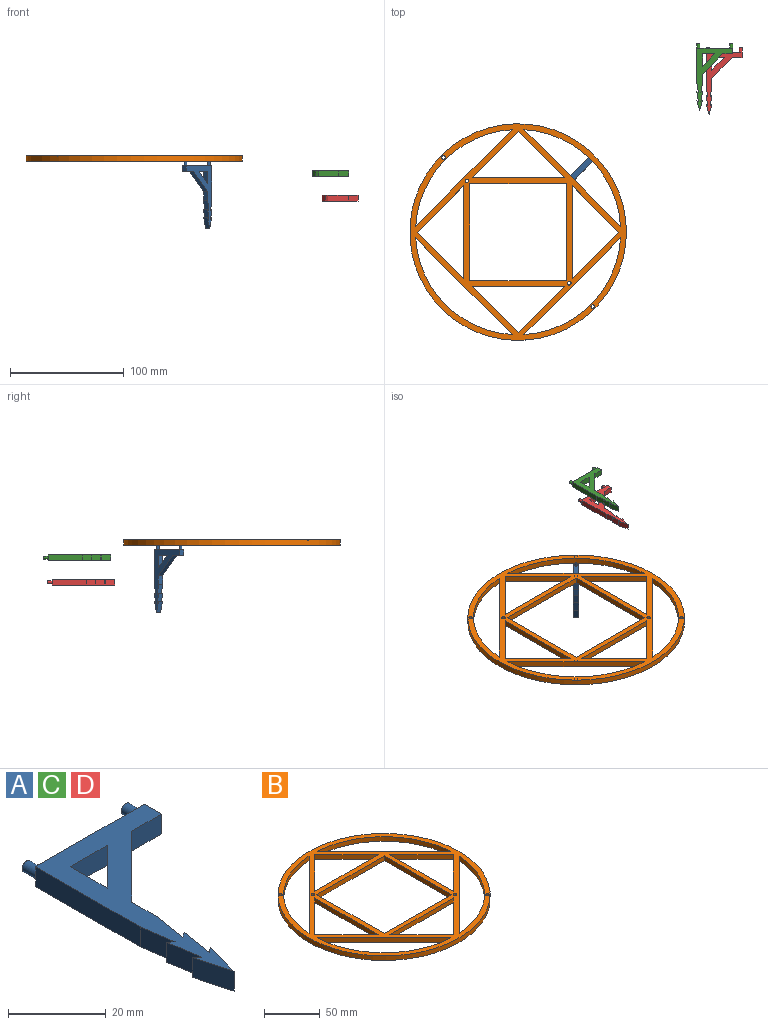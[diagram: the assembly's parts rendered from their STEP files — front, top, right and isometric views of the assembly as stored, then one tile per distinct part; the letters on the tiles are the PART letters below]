
ASSEMBLY  parts=4 mates=1
PART A: 25 faces, bbox 31.4x59x5 mm
  f0: plane 55x31.43mm, normal (0,0,1), area 463.5mm2, adj f2,f3,f4,f5,f6,f7,f8,f9
  f1: plane 55x31.43mm, normal (0,0,-1), area 463.5mm2, adj f2,f3,f4,f5,f6,f7,f8,f9
  f2: plane 7.47x5mm, normal (1,0,0), area 37.3mm2, adj f0,f1,f4,f21
  f3: plane 30.25x5mm, normal (-1,0,0), area 151.2mm2, adj f0,f1,f10,f22
  f4: plane 17.78x17.78mm, normal (0.71,-0.71,0), area 125.7mm2, adj f0,f1,f2,f5
  f5: plane 8.64x5mm, normal (0,-1,0), area 43.2mm2, adj f0,f1,f4,f6
  f6: plane 5x5mm, normal (1,0,0), area 25mm2, adj f0,f1,f5,f10
  f7: plane 10.71x5mm, normal (1,0,0), area 53.6mm2, adj f0,f1,f8,f9
  f8: plane 10.71x5mm, normal (0,-1,0), area 53.6mm2, adj f0,f1,f7,f9
  f9: plane 10.71x10.71mm, normal (-0.71,0.71,0), area 75.7mm2, adj f0,f1,f7,f8
  f10: plane 31.43x5mm, normal (0,1,0), area 146.5mm2, adj f0,f1,f3,f6,f11,f13
  f11: cylinder r=1.3mm len=4mm, axis (0,-1,0), area 32.7mm2, adj f10,f12
  f12: plane 2.6x2.6mm, normal (0,1,0), area 5.3mm2, adj f11
  f13: cylinder r=1.3mm len=4mm, axis (0,-1,0), area 32.7mm2, adj f10,f14
  f14: plane 2.6x2.6mm, normal (0,1,0), area 5.3mm2, adj f13
  f15: plane 8.81x5mm, normal (-0.99,-0.15,0), area 44.6mm2, adj f0,f1,f16,f23
  f16: plane 5x1.34mm, normal (0.67,0.74,0), area 9mm2, adj f0,f1,f15,f19
  f17: plane 5x1.38mm, normal (-0.66,0.75,0), area 9.2mm2, adj f0,f1,f18,f24
  f18: plane 8.81x5mm, normal (0.99,-0.16,0), area 44.6mm2, adj f0,f1,f17,f20
  f19: plane 9.41x5mm, normal (-0.97,-0.26,0), area 48.7mm2, adj f0,f1,f16,f24
  f20: plane 5x1.38mm, normal (-0.61,0.79,0), area 8.7mm2, adj f0,f1,f18,f21
  f21: plane 8.81x5mm, normal (0.99,-0.16,0), area 44.6mm2, adj f0,f1,f2,f20
  f22: plane 8.81x5mm, normal (-0.99,-0.15,0), area 44.6mm2, adj f0,f1,f3,f23
  f23: plane 5x1.34mm, normal (0.62,0.78,0), area 8.5mm2, adj f0,f1,f15,f22
  f24: plane 9.41x5mm, normal (0.97,-0.26,0), area 48.7mm2, adj f0,f1,f17,f19
PART B: 43 faces, bbox 190x190x5 mm
  f0: plane 190x190mm, normal (0,0,-1), area 7034.6mm2, adj f1,f2,f3,f4,f5,f6,f7,f8
  f1: plane 85x5mm, normal (0,1,0), area 425mm2, adj f0,f2,f25,f26
  f2: plane 85x5mm, normal (1,0,0), area 425mm2, adj f0,f1,f3,f26
  f3: plane 85x5mm, normal (0,-1,0), area 425mm2, adj f0,f2,f25,f26
  f4: plane 80.86x5mm, normal (-1,0,0), area 404.3mm2, adj f0,f5,f16,f26
  f5: plane 40.43x40.43mm, normal (0.71,0.71,0), area 285.9mm2, adj f0,f4,f16,f26
  f6: plane 40.43x40.43mm, normal (0.71,-0.71,0), area 285.9mm2, adj f0,f7,f17,f26
  f7: plane 40.43x40.43mm, normal (-0.71,-0.71,0), area 285.9mm2, adj f0,f6,f17,f26
  f8: cylinder r=90mm len=84.71mm, axis (0,0,-1), area 655.4mm2, adj f0,f18,f26
  f9: plane 40.43x40.43mm, normal (0.71,0.71,0), area 285.9mm2, adj f0,f10,f20,f26
  f10: plane 80.86x5mm, normal (0,-1,0), area 404.3mm2, adj f0,f9,f20,f26
  f11: cylinder r=90mm len=84.71mm, axis (0,0,-1), area 655.4mm2, adj f0,f21,f26
  f12: plane 40.43x40.43mm, normal (-0.71,-0.71,0), area 285.9mm2, adj f0,f13,f22,f26
  f13: plane 40.43x40.43mm, normal (-0.71,0.71,0), area 285.9mm2, adj f0,f12,f22,f26
  f14: cylinder r=90mm len=84.71mm, axis (0,0,-1), area 655.4mm2, adj f0,f23,f26
  f15: cylinder r=90mm len=84.71mm, axis (0,0,-1), area 655.4mm2, adj f0,f24,f26
  f16: plane 40.43x40.43mm, normal (0.71,-0.71,0), area 285.9mm2, adj f0,f4,f5,f26
  f17: plane 80.86x5mm, normal (0,1,0), area 404.3mm2, adj f0,f6,f7,f26
  f18: plane 84.71x84.71mm, normal (-0.71,0.71,0), area 599mm2, adj f0,f8,f26
  f19: cylinder r=95mm len=190mm, axis (0,0,-1), area 2984.5mm2, adj f0,f26
  f20: plane 40.43x40.43mm, normal (-0.71,0.71,0), area 285.9mm2, adj f0,f9,f10,f26
  f21: plane 84.71x84.71mm, normal (-0.71,-0.71,0), area 599mm2, adj f0,f11,f26
  f22: plane 80.86x5mm, normal (1,0,0), area 404.3mm2, adj f0,f12,f13,f26
  f23: plane 84.71x84.71mm, normal (0.71,0.71,0), area 599mm2, adj f0,f14,f26
  f24: plane 84.71x84.71mm, normal (0.71,-0.71,0), area 599mm2, adj f0,f15,f26
  f25: plane 85x5mm, normal (-1,0,0), area 425mm2, adj f0,f1,f3,f26
  f26: plane 190x190mm, normal (0,0,1), area 7062.8mm2, adj f1,f2,f3,f4,f5,f6,f7,f8
  f27: cylinder r=1.5mm len=4mm, axis (0,0,-1), area 35.1mm2, adj f0,f28,f29
  f28: plane 4x0.46mm, normal (0.71,0.71,0), area 2.6mm2, adj f0,f27,f29
  f29: plane 3x3mm, normal (0,0,-1), area 7.1mm2, adj f27,f28
  f30: cylinder r=1.5mm len=4mm, axis (0,0,-1), area 35.1mm2, adj f0,f31,f32
  f31: plane 4x0.46mm, normal (-0.71,-0.71,0), area 2.6mm2, adj f0,f30,f32
  f32: plane 3x3mm, normal (0,0,-1), area 7.1mm2, adj f30,f31
  f33: cylinder r=1.5mm len=4mm, axis (0,0,-1), area 37.7mm2, adj f0,f34
  f34: plane 3x3mm, normal (0,0,-1), area 7.1mm2, adj f33
  f35: cylinder r=1.5mm len=4mm, axis (0,0,-1), area 37.7mm2, adj f0,f36
  f36: plane 3x3mm, normal (0,0,-1), area 7.1mm2, adj f35
  f37: cylinder r=1.5mm len=5mm, axis (0,0,-1), area 47.1mm2, adj f0,f26
  f38: cylinder r=1.5mm len=5mm, axis (0,0,-1), area 43.9mm2, adj f0,f26,f39
  f39: plane 5x0.46mm, normal (0.71,-0.71,0), area 3.2mm2, adj f0,f26,f38
  f40: cylinder r=1.5mm len=5mm, axis (0,0,-1), area 43.9mm2, adj f0,f26,f41
  f41: plane 5x0.46mm, normal (-0.71,0.71,0), area 3.2mm2, adj f0,f26,f40
  f42: cylinder r=1.5mm len=5mm, axis (0,0,-1), area 47.1mm2, adj f0,f26
PART C: same geometry as A
PART D: same geometry as A
PLACE A rot(axis=(0.28,-0.68,-0.68),148.6deg) t=(5.53,9.81,-146.04)mm
PLACE B t=(-48.12,-40.3,-47.68)mm
PLACE C t=(129.1,26.63,-61.08)mm
PLACE D t=(137.3,23.25,-82.68)mm
MATE fastened A.f13 <-> B.f33  axis (0,0,1) through (17.29,25.1,-47.68)mm
